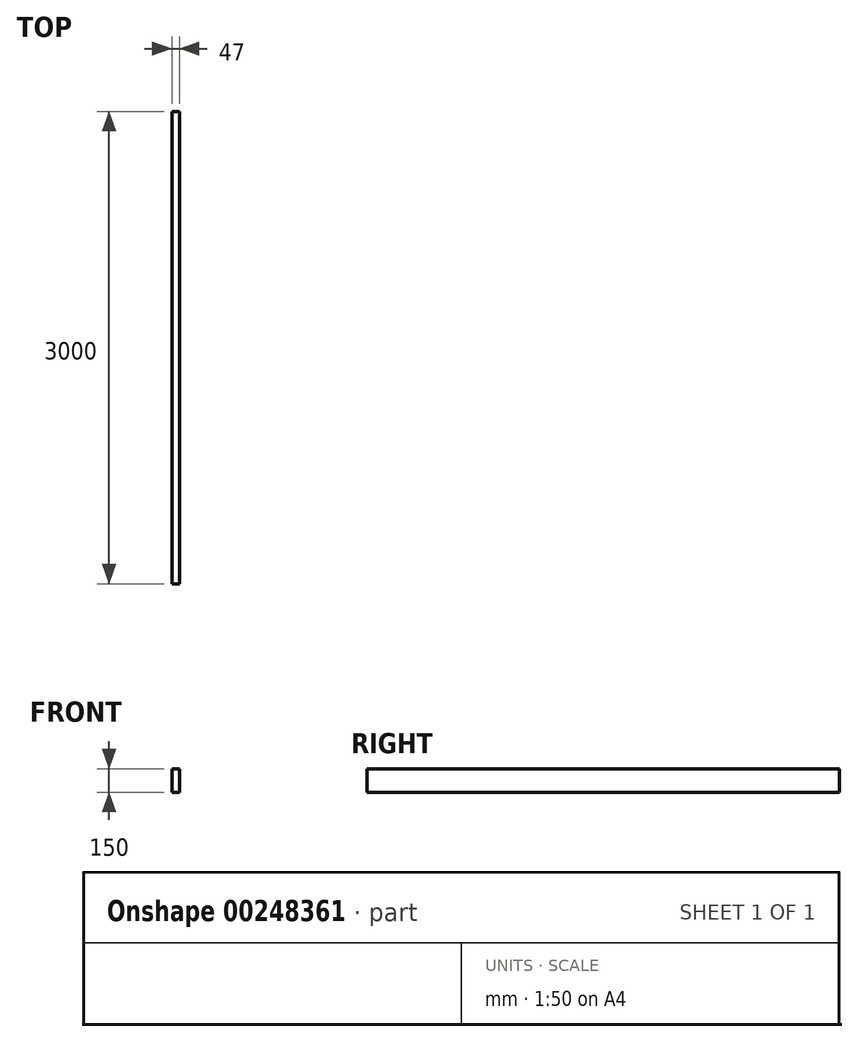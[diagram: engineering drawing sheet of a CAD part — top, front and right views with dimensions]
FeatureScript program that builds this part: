
annotation { "Feature Type Name" : "Feature", "Feature Type Description" : "" }
export const myFeature = defineFeature(function(context is Context, id is Id, definition is map)
    precondition{}
    {
        {
            var Q0;
            Q0=qCreatedBy(makeId("Front.planeOp"),FACE);
            var sketch = newSketch(context, id + "F0", { "sketchPlane" : qUnion([Q0])});
            skLineSegment(sketch, "E0.bottom", {"start": v(0, 0) * mm, "end": v(47, 0) * mm});
            skLineSegment(sketch, "E0.top", {"start": v(0, 150) * mm, "end": v(47, 150) * mm});
            skLineSegment(sketch, "E0.left", {"start": v(0, 0) * mm, "end": v(0, 150) * mm});
            skLineSegment(sketch, "E0.right", {"start": v(47, 0) * mm, "end": v(47, 150) * mm});
            skSolve(sketch);
        }
        {
            var Q0;
            Q0 = qSketchRegion(id + "F0", true);
            extrude(context, id + "F1", {"entities" : qUnion([Q0]), "oppositeDirection" : true, "depth" : 3000 * mm});
        }
    });
